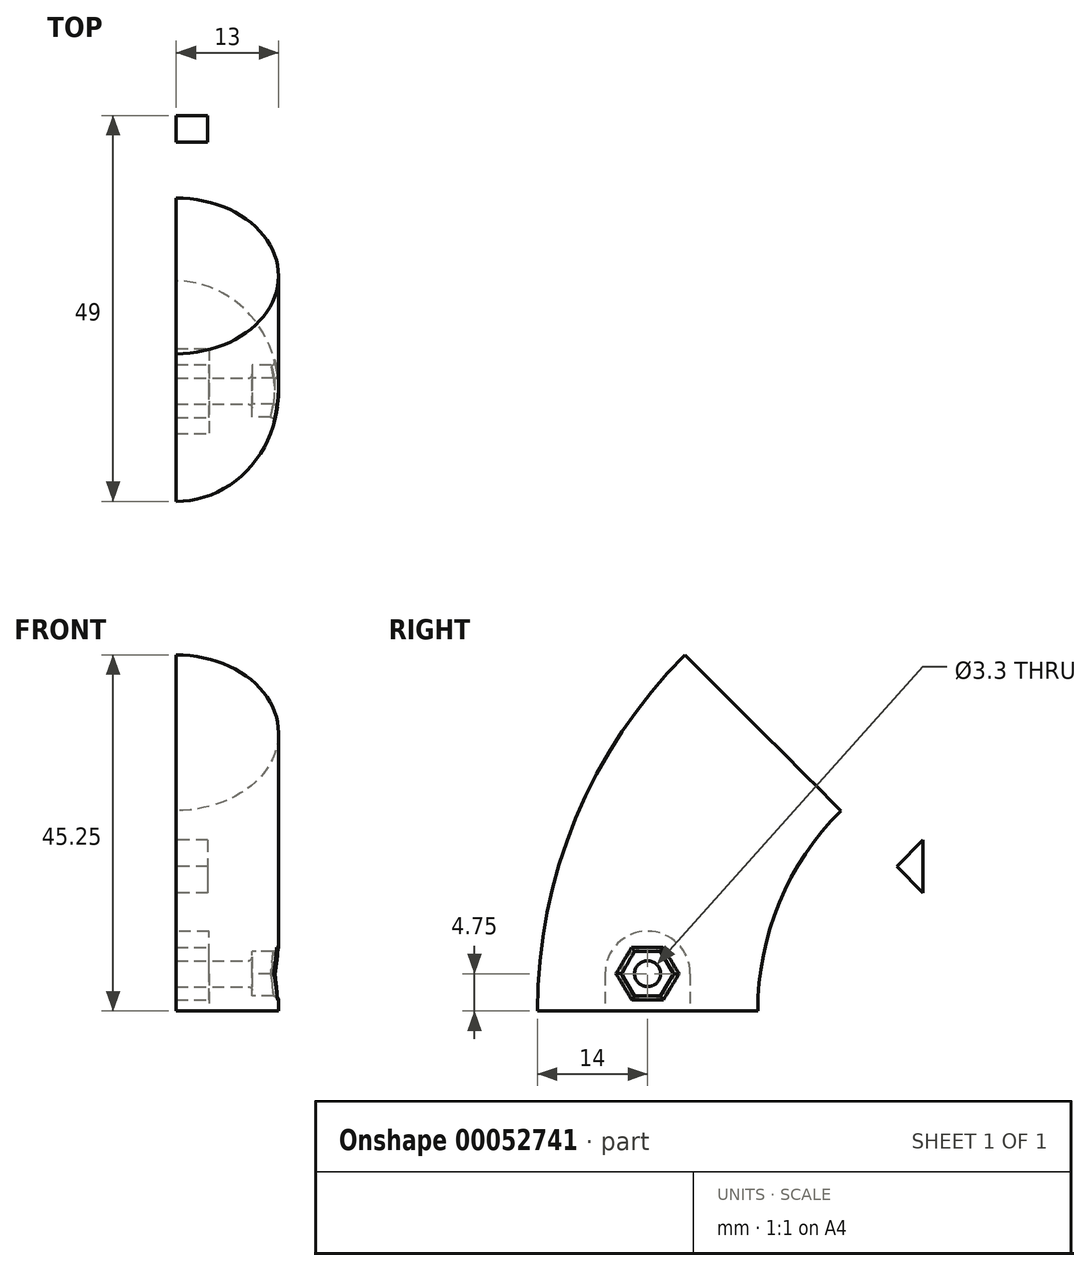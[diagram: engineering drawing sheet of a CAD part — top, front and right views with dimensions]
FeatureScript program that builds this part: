
annotation { "Feature Type Name" : "Feature", "Feature Type Description" : "" }
export const myFeature = defineFeature(function(context is Context, id is Id, definition is map)
    precondition{}
    {
        {
            var Q0;
            Q0=qCreatedBy(makeId("Top.planeOp"),FACE);
            var sketch = newSketch(context, id + "F0", { "sketchPlane" : qUnion([Q0])});
            skEllipse(sketch, "E0", {"center": v(0, 0) * mm, "majorRadius": 14 * mm, "minorRadius": 13 * mm, "majorAxis": v(0, 1)});
            skLineSegment(sketch, "E1", {"start": v(0, 0) * mm, "end": v(0, 50) * mm, "construction": true});
            skLineSegment(sketch, "E2", {"start": v(0, 50) * mm, "end": v(27.53, 50) * mm, "construction": true});
            skLineSegment(sketch, "E3.rect.bottom", {"start": v(-4.15, 5.4) * mm, "end": v(4.15, 5.4) * mm});
            skLineSegment(sketch, "E3.rect.top", {"start": v(-4.15, -5.4) * mm, "end": v(4.15, -5.4) * mm});
            skLineSegment(sketch, "E3.rect.left", {"start": v(-4.15, 5.4) * mm, "end": v(-4.15, -5.4) * mm});
            skLineSegment(sketch, "E3.rect.right", {"start": v(4.15, 5.4) * mm, "end": v(4.15, -5.4) * mm});
            skSolve(sketch);
        }
        {
            var Q0;
            Q0=makeQuery(id+"F0.imprint","IMPRINT",FACE,{"disambiguationData":[TD([[makeQuery(id+"F0.imprint","IMPRINT",EDGE,{"derivedFrom":sQuery(id+"F0.wireOp",EDGE,"E0")}),1.0]])]});
            var Q1;
            Q1=makeQuery(id+"F0.imprint","IMPRINT",FACE,{"disambiguationData":[TD([[makeQuery(id+"F0.imprint","IMPRINT",EDGE,{"derivedFrom":sQuery(id+"F0.wireOp",EDGE,"E3.rect.bottom")}),-1.0]])]});
            var Q2;
            Q2=sQuery(id+"F0.wireOp",EDGE,"E2");
            revolve(context, id + "F1", {"entities" : qUnion([Q0, Q1]), "axis" : qUnion([Q2]), "revolveType" : RevolveType.ONE_DIRECTION, "oppositeDirection" : true, "angle" : 45 * degree});
        }
        {
            var Q0;
            Q0=makeQuery(id+"F1.opRevolve","CAP_FACE",FACE,{"disambiguationData":[OSD([sQuery(id+"F0.wireOp",EDGE,"E0")])],"isStart":false});
            var sketch = newSketch(context, id + "F2", { "sketchPlane" : qUnion([Q0])});
            skLineSegment(sketch, "E4.rect.bottom", {"start": v(-4, -9.4) * mm, "end": v(4, -9.4) * mm});
            skLineSegment(sketch, "E4.rect.top", {"start": v(-4, -19.9) * mm, "end": v(4, -19.9) * mm});
            skLineSegment(sketch, "E4.rect.left", {"start": v(-4, -9.4) * mm, "end": v(-4, -19.9) * mm});
            skLineSegment(sketch, "E4.rect.right", {"start": v(4, -9.4) * mm, "end": v(4, -19.9) * mm});
            skPoint(sketch, "E4.rect.middle", {"position": v(0, -14.64) * mm});
            skLineSegment(sketch, "E5", {"start": v(0, -0.64) * mm, "end": v(0, -14.64) * mm, "construction": true});
            skPoint(sketch, "E6.orphan", {"position": v(0, -28.64) * mm});
            skSolve(sketch);
        }
        {
            var Q0;
            Q0=makeQuery(id+"F2.imprint","IMPRINT",FACE,{"disambiguationData":[TD([[makeQuery(id+"F2.imprint","IMPRINT",EDGE,{"derivedFrom":sQuery(id+"F2.wireOp",EDGE,"E4.rect.bottom")}),-1.0]])]});
            extrude(context, id + "F3", {"entities" : qUnion([Q0]), "operationType" : NewBodyOperationType.ADD, "depth" : 10 * mm});
        }
        {
            var Q0;
            Q0=makeQuery(id+"F3.opExtrude","CAP_EDGE",EDGE,{"disambiguationData":[OSD([sQuery(id+"F2.wireOp",EDGE,"E4.rect.top")])],"isStart":false});
            var Q1;
            Q1=makeQuery(id+"F3.opExtrude","CAP_EDGE",EDGE,{"disambiguationData":[OSD([sQuery(id+"F2.wireOp",EDGE,"E4.rect.bottom")])],"isStart":false});
            fillet(context, id + "F4", {"entities" : qUnion([Q0, Q1]), "radius" : 5.25 * mm, "tangentPropagation" : true, "allowEdgeOverflow" : false});
        }
        {
            var Q0;
            Q0=makeQuery(id+"F3.opExtrude","SWEPT_FACE",FACE,{"disambiguationData":[OSD([sQuery(id+"F2.wireOp",EDGE,"E4.rect.right")])]});
            var sketch = newSketch(context, id + "F5", { "sketchPlane" : qUnion([Q0])});
            skLineSegment(sketch, "E7", {"start": v(14.64, 35.36) * mm, "end": v(18, 38.71) * mm, "construction": true});
            skCircle(sketch, "E8", {"center": v(18, 38.71) * mm, "radius": 3.5 * mm});
            skSolve(sketch);
        }
        {
            var Q0;
            Q0 = qSketchRegion(id + "F5", true);
            extrude(context, id + "F6", {"entities" : qUnion([Q0]), "operationType" : NewBodyOperationType.REMOVE, "endBound" : BoundingType.THROUGH_ALL, "oppositeDirection" : true, "depth" : 25 * mm});
        }
        {
            var Q0;
            Q0=makeQuery(id+"F0.imprint","IMPRINT",FACE,{"disambiguationData":[TD([[makeQuery(id+"F0.imprint","IMPRINT",EDGE,{"derivedFrom":sQuery(id+"F0.wireOp",EDGE,"E3.rect.bottom")}),-1.0]])]});
            extrude(context, id + "F7", {"entities" : qUnion([Q0]), "operationType" : NewBodyOperationType.REMOVE, "depth" : 10.15 * mm});
        }
        {
            var Q0;
            Q0=makeQuery(id+"F7.boolean.opBoolean","COPY",EDGE,{"derivedFrom":makeQuery(id+"F7.opExtrude","CAP_EDGE",EDGE,{"disambiguationData":[OSD([sQuery(id+"F0.wireOp",EDGE,"E3.rect.bottom")])],"isStart":false})});
            var Q1;
            Q1=makeQuery(id+"F7.boolean.opBoolean","COPY",EDGE,{"derivedFrom":makeQuery(id+"F7.opExtrude","CAP_EDGE",EDGE,{"disambiguationData":[OSD([sQuery(id+"F0.wireOp",EDGE,"E3.rect.top")])],"isStart":false})});
            fillet(context, id + "F8", {"entities" : qUnion([Q0, Q1]), "radius" : 5.4 * mm, "tangentPropagation" : true, "allowEdgeOverflow" : false});
        }
        {
            var Q0;
            Q0=qCreatedBy(makeId("Top.planeOp"),FACE);
            var sketch = newSketch(context, id + "F9", { "sketchPlane" : qUnion([Q0])});
            skLineSegment(sketch, "E9.bottom", {"start": v(0, 35) * mm, "end": v(20, 35) * mm});
            skLineSegment(sketch, "E9.top", {"start": v(0, -35) * mm, "end": v(20, -35) * mm});
            skLineSegment(sketch, "E9.left", {"start": v(0, 35) * mm, "end": v(0, -35) * mm});
            skLineSegment(sketch, "E9.right", {"start": v(20, 35) * mm, "end": v(20, -35) * mm});
            skLineSegment(sketch, "E10", {"start": v(20, 35) * mm, "end": v(20, 0) * mm, "construction": true});
            skSolve(sketch);
        }
        {
            var Q0;
            Q0 = qSketchRegion(id + "F9", true);
            extrude(context, id + "F10", {"entities" : qUnion([Q0]), "operationType" : NewBodyOperationType.INTERSECT, "depth" : 50 * mm});
        }
        {
            var Q0;
            Q0=makeQuery(id+"F7.boolean.opBoolean","COPY",FACE,{"derivedFrom":makeQuery(id+"F7.opExtrude","SWEPT_FACE",FACE,{"disambiguationData":[OSD([sQuery(id+"F0.wireOp",EDGE,"E3.rect.right")])]})});
            var sketch = newSketch(context, id + "F11", { "sketchPlane" : qUnion([Q0])});
            skCircle(sketch, "E11", {"center": v(0, 4.75) * mm, "radius": 3.35 * mm});
            skCircle(sketch, "E12", {"center": v(0, 4.75) * mm, "radius": 1.65 * mm});
            skSolve(sketch);
        }
        {
            var Q0;
            Q0=makeQuery(id+"F11.imprint","IMPRINT",FACE,{"disambiguationData":[TD([[makeQuery(id+"F11.imprint","IMPRINT",EDGE,{"derivedFrom":sQuery(id+"F11.wireOp",EDGE,"E11")}),1.0]])]});
            var Q1;
            Q1=makeQuery(id+"F1.opRevolve","SWEPT_BODY",BODY,{"disambiguationData":[OSD([sQuery(id+"F0.wireOp",EDGE,"E0")])]});
            extrude(context, id + "F12", {"entities" : qUnion([Q0]), "operationType" : NewBodyOperationType.ADD, "endBoundEntityBody" : qUnion([Q1]), "depth" : 4.15 * mm});
        }
        {
            var Q0;
            Q0=makeQuery(id+"F12.boolean.opBoolean","SPLIT",FACE,{"disambiguationData":[TD([makeQuery(id+"F12.opExtrude","SWEPT_FACE",FACE,{"disambiguationData":[OSD([sQuery(id+"F11.wireOp",EDGE,"E12")])]})])],"derivedFrom":makeQuery(id+"F7.boolean.opBoolean","COPY",FACE,{"derivedFrom":makeQuery(id+"F7.opExtrude","SWEPT_FACE",FACE,{"disambiguationData":[OSD([sQuery(id+"F0.wireOp",EDGE,"E3.rect.right")])]})})});
            extrude(context, id + "F13", {"entities" : qUnion([Q0]), "operationType" : NewBodyOperationType.REMOVE, "oppositeDirection" : true, "depth" : 25 * mm});
        }
        {
            var Q0;
            Q0=makeQuery(id+"F12.boolean.opBoolean","SPLIT",FACE,{"disambiguationData":[TD([makeQuery(id+"F1.opRevolve","CAP_FACE",FACE,{"disambiguationData":[OSD([sQuery(id+"F0.wireOp",EDGE,"E0")])],"isStart":true})])],"derivedFrom":makeQuery(id+"F7.boolean.opBoolean","COPY",FACE,{"derivedFrom":makeQuery(id+"F7.opExtrude","SWEPT_FACE",FACE,{"disambiguationData":[OSD([sQuery(id+"F0.wireOp",EDGE,"E3.rect.right")])]})})});
            var sketch = newSketch(context, id + "F14", { "sketchPlane" : qUnion([Q0])});
            skCircle(sketch, "E13.cCircle", {"center": v(0, 4.75) * mm, "radius": 2.85 * mm, "construction": true});
            skLineSegment(sketch, "E13.0", {"start": v(-1.65, 7.6) * mm, "end": v(1.65, 7.6) * mm});
            skLineSegment(sketch, "E13.1", {"start": v(1.65, 7.6) * mm, "end": v(3.3, 4.75) * mm});
            skLineSegment(sketch, "E13.2", {"start": v(3.3, 4.75) * mm, "end": v(1.65, 1.9) * mm});
            skLineSegment(sketch, "E13.3", {"start": v(1.65, 1.9) * mm, "end": v(-1.65, 1.9) * mm});
            skLineSegment(sketch, "E13.4", {"start": v(-1.65, 1.9) * mm, "end": v(-3.3, 4.75) * mm});
            skLineSegment(sketch, "E13.5", {"start": v(-3.3, 4.75) * mm, "end": v(-1.65, 7.6) * mm});
            skPoint(sketch, "E13.0.midPoint", {"position": v(0, 7.6) * mm});
            skCircle(sketch, "E14", {"center": v(0, 4.75) * mm, "radius": 1.65 * mm});
            skSolve(sketch);
        }
        {
            var Q0;
            Q0 = qSketchRegion(id + "F14", true);
            extrude(context, id + "F15", {"entities" : qUnion([Q0]), "operationType" : NewBodyOperationType.REMOVE, "oppositeDirection" : true, "depth" : 25 * mm});
        }
        {
            var Q0;
            Q0 = qSketchRegion(id + "F14", true);
            extrude(context, id + "F16", {"entities" : qUnion([Q0]), "operationType" : NewBodyOperationType.ADD, "oppositeDirection" : true, "depth" : 5.5 * mm});
        }
        {
            var Q0;
            Q0=makeQuery(id+"F15.boolean.opBoolean","INTERSECT",EDGE,{"derivedFrom":[makeQuery(id+"F1.opRevolve","SWEPT_FACE",FACE,{"disambiguationData":[OSD([sQuery(id+"F0.wireOp",EDGE,"E0")])]}),makeQuery(id+"F15.opExtrude","SWEPT_FACE",FACE,{"disambiguationData":[OSD([sQuery(id+"F14.wireOp",EDGE,"E13.3")])]})]});
            var Q1;
            Q1=makeQuery(id+"F15.boolean.opBoolean","INTERSECT",EDGE,{"derivedFrom":[makeQuery(id+"F1.opRevolve","SWEPT_FACE",FACE,{"disambiguationData":[OSD([sQuery(id+"F0.wireOp",EDGE,"E0")])]}),makeQuery(id+"F15.opExtrude","SWEPT_FACE",FACE,{"disambiguationData":[OSD([sQuery(id+"F14.wireOp",EDGE,"E13.2")])]})]});
            var Q2;
            Q2=makeQuery(id+"F15.boolean.opBoolean","INTERSECT",EDGE,{"derivedFrom":[makeQuery(id+"F1.opRevolve","SWEPT_FACE",FACE,{"disambiguationData":[OSD([sQuery(id+"F0.wireOp",EDGE,"E0")])]}),makeQuery(id+"F15.opExtrude","SWEPT_FACE",FACE,{"disambiguationData":[OSD([sQuery(id+"F14.wireOp",EDGE,"E13.1")])]})]});
            var Q3;
            Q3=makeQuery(id+"F15.boolean.opBoolean","INTERSECT",EDGE,{"derivedFrom":[makeQuery(id+"F1.opRevolve","SWEPT_FACE",FACE,{"disambiguationData":[OSD([sQuery(id+"F0.wireOp",EDGE,"E0")])]}),makeQuery(id+"F15.opExtrude","SWEPT_FACE",FACE,{"disambiguationData":[OSD([sQuery(id+"F14.wireOp",EDGE,"E13.0")])]})]});
            var Q4;
            Q4=makeQuery(id+"F15.boolean.opBoolean","INTERSECT",EDGE,{"derivedFrom":[makeQuery(id+"F1.opRevolve","SWEPT_FACE",FACE,{"disambiguationData":[OSD([sQuery(id+"F0.wireOp",EDGE,"E0")])]}),makeQuery(id+"F15.opExtrude","SWEPT_FACE",FACE,{"disambiguationData":[OSD([sQuery(id+"F14.wireOp",EDGE,"E13.5")])]})]});
            var Q5;
            Q5=makeQuery(id+"F15.boolean.opBoolean","INTERSECT",EDGE,{"derivedFrom":[makeQuery(id+"F1.opRevolve","SWEPT_FACE",FACE,{"disambiguationData":[OSD([sQuery(id+"F0.wireOp",EDGE,"E0")])]}),makeQuery(id+"F15.opExtrude","SWEPT_FACE",FACE,{"disambiguationData":[OSD([sQuery(id+"F14.wireOp",EDGE,"E13.4")])]})]});
            var Q6;
            Q6=makeQuery(id+"F16.opExtrude","CAP_EDGE",EDGE,{"disambiguationData":[OSD([sQuery(id+"F14.wireOp",EDGE,"E14")])],"isStart":false});
            fillet(context, id + "F17", {"entities" : qUnion([Q0, Q1, Q2, Q3, Q4, Q5, Q6]), "radius" : 0.5 * mm, "tangentPropagation" : true, "allowEdgeOverflow" : false});
        }
    });
